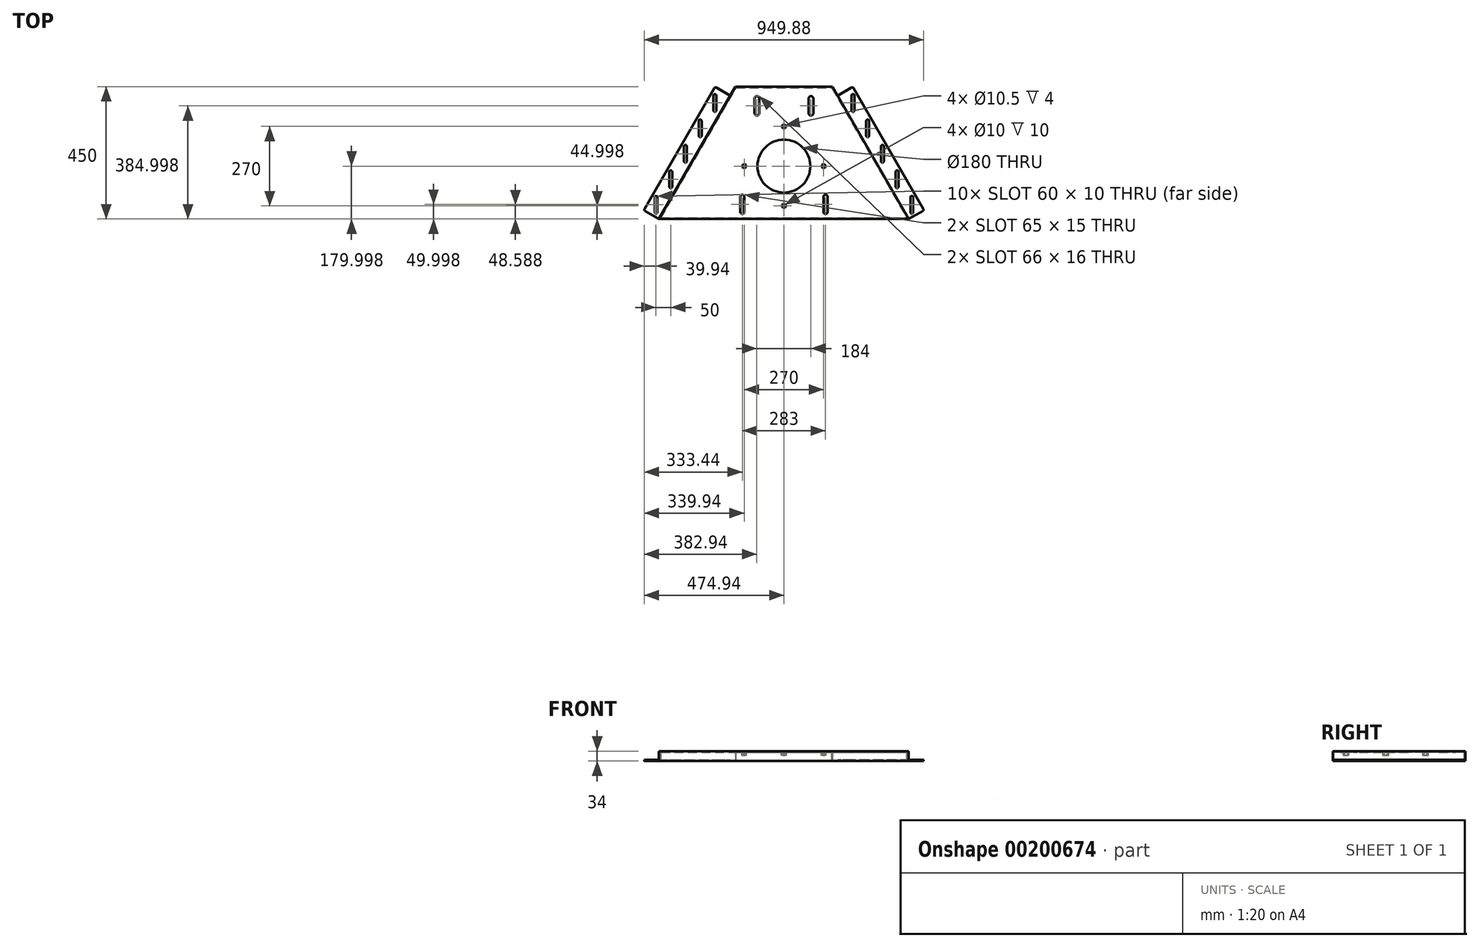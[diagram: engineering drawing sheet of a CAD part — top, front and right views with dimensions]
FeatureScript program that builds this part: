
annotation { "Feature Type Name" : "Feature", "Feature Type Description" : "" }
export const myFeature = defineFeature(function(context is Context, id is Id, definition is map)
    precondition{}
    {
        {
            var Q0;
            Q0=qCreatedBy(makeId("Top.planeOp"),FACE);
            var sketch = newSketch(context, id + "F0", { "sketchPlane" : qUnion([Q0])});
            skLineSegment(sketch, "E0.bottom", {"start": v(0, -344.4) * mm, "end": v(-424.8, -344.4) * mm});
            skLineSegment(sketch, "E0.top", {"start": v(0, 105.6) * mm, "end": v(-165, 105.6) * mm});
            skLineSegment(sketch, "E0.right", {"start": v(-424.8, -344.4) * mm, "end": v(-165, 105.6) * mm});
            skPoint(sketch, "E0.middle", {"position": v(0, 0) * mm});
            skLineSegment(sketch, "E1", {"start": v(0, 0) * mm, "end": v(0, 211.2) * mm, "construction": true});
            skLineSegment(sketch, "E2.MirrorCS", {"start": v(0, 105.6) * mm, "end": v(165, 105.6) * mm});
            skLineSegment(sketch, "E3.MirrorCS", {"start": v(424.8, -344.4) * mm, "end": v(165, 105.6) * mm});
            skLineSegment(sketch, "E4.MirrorCS", {"start": v(0, -344.4) * mm, "end": v(424.8, -344.4) * mm});
            skSolve(sketch);
        }
        {
            var Q0;
            Q0 = qSketchRegion(id + "F0", true);
            extrude(context, id + "F1", {"entities" : qUnion([Q0]), "depth" : 4 * mm});
        }
        {
            var Q0;
            Q0=makeQuery(id+"F1.opExtrude","CAP_FACE",FACE,{"disambiguationData":[OSD([sQuery(id+"F0.wireOp",EDGE,"E0.bottom"),sQuery(id+"F0.wireOp",EDGE,"E0.top"),sQuery(id+"F0.wireOp",EDGE,"E0.left"),sQuery(id+"F0.wireOp",EDGE,"E0.right")])],"isStart":false});
            var sketch = newSketch(context, id + "F2", { "sketchPlane" : qUnion([Q0])});
            skLineSegment(sketch, "E5", {"start": v(0, 105.6) * mm, "end": v(0, -344.4) * mm, "construction": true});
            skCircle(sketch, "E6", {"center": v(0, -29.4) * mm, "radius": 5.25 * mm});
            skLineSegment(sketch, "E7", {"start": v(-320.88, -164.4) * mm, "end": v(320.88, -164.4) * mm, "construction": true});
            skCircle(sketch, "E8.MirrorC", {"center": v(0, -299.4) * mm, "radius": 5.25 * mm});
            skCircle(sketch, "E9", {"center": v(-135, -164.4) * mm, "radius": 5.25 * mm});
            skCircle(sketch, "E10.MirrorC", {"center": v(135, -164.4) * mm, "radius": 5.25 * mm});
            skCircle(sketch, "E11", {"center": v(0, -164.4) * mm, "radius": 90 * mm});
            skLineSegment(sketch, "E12.bottom", {"start": v(-84, 15.6) * mm, "end": v(-100, 15.6) * mm});
            skLineSegment(sketch, "E12.top", {"start": v(-84, 65.6) * mm, "end": v(-100, 65.6) * mm});
            skLineSegment(sketch, "E12.left", {"start": v(-84, 15.6) * mm, "end": v(-84, 65.6) * mm});
            skLineSegment(sketch, "E12.right", {"start": v(-100, 15.6) * mm, "end": v(-100, 65.6) * mm});
            skPoint(sketch, "E12.middle", {"position": v(-92, 40.6) * mm});
            skLineSegment(sketch, "E13.MirrorCS", {"start": v(84, 15.6) * mm, "end": v(100, 15.6) * mm});
            skLineSegment(sketch, "E14.MirrorCS", {"start": v(84, 65.6) * mm, "end": v(100, 65.6) * mm});
            skLineSegment(sketch, "E15.MirrorCS", {"start": v(100, 15.6) * mm, "end": v(100, 65.6) * mm});
            skLineSegment(sketch, "E16.MirrorCS", {"start": v(84, 15.6) * mm, "end": v(84, 65.6) * mm});
            skPoint(sketch, "E17.MirrorP", {"position": v(92, 40.6) * mm});
            skArc(sketch, "E18", {"start": v(-84, 65.6) * mm, "mid": v(-92, 73.6) * mm, "end": v(-100, 65.6) * mm});
            skArc(sketch, "E19", {"start": v(-100, 15.6) * mm, "mid": v(-92, 7.6) * mm, "end": v(-84, 15.6) * mm});
            skArc(sketch, "E20.MirrorCS", {"start": v(84, 65.6) * mm, "mid": v(92, 73.6) * mm, "end": v(100, 65.6) * mm});
            skArc(sketch, "E21.MirrorCS", {"start": v(100, 15.6) * mm, "mid": v(92, 7.6) * mm, "end": v(84, 15.6) * mm});
            skSolve(sketch);
        }
        {
            var Q0;
            Q0 = qSketchRegion(id + "F2", true);
            extrude(context, id + "F3", {"entities" : qUnion([Q0]), "operationType" : NewBodyOperationType.REMOVE, "oppositeDirection" : true, "depth" : 25 * mm});
        }
        {
            var Q0;
            Q0=makeQuery(id+"F1.opExtrude","CAP_FACE",FACE,{"disambiguationData":[OSD([sQuery(id+"F0.wireOp",EDGE,"E0.bottom"),sQuery(id+"F0.wireOp",EDGE,"E0.top"),sQuery(id+"F0.wireOp",EDGE,"E0.left"),sQuery(id+"F0.wireOp",EDGE,"E0.right")])],"isStart":true});
            var sketch = newSketch(context, id + "F4", { "sketchPlane" : qUnion([Q0])});
            skLineSegment(sketch, "E22.bottom", {"start": v(-165, -105.6) * mm, "end": v(165, -105.6) * mm});
            skLineSegment(sketch, "E22.top", {"start": v(-165, -101.6) * mm, "end": v(165, -101.6) * mm});
            skLineSegment(sketch, "E22.left", {"start": v(-165, -105.6) * mm, "end": v(-165, -101.6) * mm});
            skLineSegment(sketch, "E22.right", {"start": v(165, -105.6) * mm, "end": v(165, -101.6) * mm});
            skLineSegment(sketch, "E23.bottom", {"start": v(-424.8, 344.4) * mm, "end": v(424.8, 344.4) * mm});
            skLineSegment(sketch, "E23.top", {"start": v(-422.5, 340.4) * mm, "end": v(422.5, 340.4) * mm});
            skLineSegment(sketch, "E23.left", {"start": v(-424.8, 344.4) * mm, "end": v(-422.5, 340.4) * mm});
            skLineSegment(sketch, "E24.bottom", {"start": v(-423.65, 342.4) * mm, "end": v(-420.19, 344.4) * mm});
            skLineSegment(sketch, "E24.top", {"start": v(-165, -105.6) * mm, "end": v(-161.54, -103.6) * mm});
            skLineSegment(sketch, "E24.left", {"start": v(-423.65, 342.4) * mm, "end": v(-165, -105.6) * mm});
            skLineSegment(sketch, "E24.right", {"start": v(-420.19, 344.4) * mm, "end": v(-161.54, -103.6) * mm});
            skLineSegment(sketch, "E25.bottom", {"start": v(161.54, -103.6) * mm, "end": v(165, -105.6) * mm});
            skLineSegment(sketch, "E25.left", {"start": v(165, -105.6) * mm, "end": v(424.8, 344.4) * mm});
            skLineSegment(sketch, "E25.right", {"start": v(161.54, -103.6) * mm, "end": v(420.19, 344.4) * mm});
            skSolve(sketch);
        }
        {
            var Q0;
            Q0 = qSketchRegion(id + "F4", true);
            extrude(context, id + "F5", {"entities" : qUnion([Q0]), "operationType" : NewBodyOperationType.ADD, "depth" : 30 * mm});
        }
        {
            var Q0;
            Q0=makeQuery(id+"F5.opExtrude","CAP_FACE",FACE,{"disambiguationData":[OSD([sQuery(id+"F4.wireOp",EDGE,"E22.bottom"),sQuery(id+"F4.wireOp",EDGE,"E22.top"),sQuery(id+"F4.wireOp",EDGE,"E23.bottom"),sQuery(id+"F4.wireOp",EDGE,"E23.top"),sQuery(id+"F4.wireOp",EDGE,"E23.left"),sQuery(id+"F4.wireOp",EDGE,"E23.right"),sQuery(id+"F4.wireOp",EDGE,"E24.bottom"),sQuery(id+"F4.wireOp",EDGE,"E24.left"),sQuery(id+"F4.wireOp",EDGE,"E24.right"),sQuery(id+"F4.wireOp",EDGE,"E25.top"),sQuery(id+"F4.wireOp",EDGE,"E25.left"),sQuery(id+"F4.wireOp",EDGE,"E25.right")])],"isStart":false});
            var sketch = newSketch(context, id + "F6", { "sketchPlane" : qUnion([Q0])});
            skLineSegment(sketch, "E26.bottom", {"start": v(-476.77, 314.4) * mm, "end": v(-424.8, 344.4) * mm});
            skLineSegment(sketch, "E26.top", {"start": v(-234.28, -105.6) * mm, "end": v(-182.32, -75.6) * mm});
            skLineSegment(sketch, "E26.left", {"start": v(-476.77, 314.4) * mm, "end": v(-234.28, -105.6) * mm});
            skLineSegment(sketch, "E26.right", {"start": v(-424.8, 344.4) * mm, "end": v(-182.32, -75.6) * mm});
            skLineSegment(sketch, "E27", {"start": v(-165, -105.6) * mm, "end": v(-269.69, -105.6) * mm, "construction": true});
            skLineSegment(sketch, "E28", {"start": v(0, 340.4) * mm, "end": v(0, 72.27) * mm, "construction": true});
            skPoint(sketch, "E28.endSnap0", {"position": v(0, -101.6) * mm});
            skLineSegment(sketch, "E29.MirrorCS", {"start": v(476.77, 314.4) * mm, "end": v(234.28, -105.6) * mm});
            skLineSegment(sketch, "E30.MirrorCS", {"start": v(424.8, 344.4) * mm, "end": v(182.32, -75.6) * mm});
            skLineSegment(sketch, "E31.MirrorCS", {"start": v(234.28, -105.6) * mm, "end": v(182.32, -75.6) * mm});
            skLineSegment(sketch, "E32.MirrorCS", {"start": v(476.77, 314.4) * mm, "end": v(424.8, 344.4) * mm});
            skSolve(sketch);
        }
        {
            var Q0;
            Q0 = qSketchRegion(id + "F6", true);
            extrude(context, id + "F7", {"entities" : qUnion([Q0]), "operationType" : NewBodyOperationType.ADD, "oppositeDirection" : true, "depth" : 4 * mm});
        }
        {
            var Q0;
            Q0=makeQuery(id+"F7.boolean.opBoolean","MERGE",FACE,{"derivedFrom":[makeQuery(id+"F5.opExtrude","CAP_FACE",FACE,{"disambiguationData":[OSD([sQuery(id+"F4.wireOp",EDGE,"E22.bottom"),sQuery(id+"F4.wireOp",EDGE,"E22.top"),sQuery(id+"F4.wireOp",EDGE,"E23.bottom"),sQuery(id+"F4.wireOp",EDGE,"E23.top"),sQuery(id+"F4.wireOp",EDGE,"E23.left"),sQuery(id+"F4.wireOp",EDGE,"E23.right"),sQuery(id+"F4.wireOp",EDGE,"E24.bottom"),sQuery(id+"F4.wireOp",EDGE,"E24.left"),sQuery(id+"F4.wireOp",EDGE,"E24.right"),sQuery(id+"F4.wireOp",EDGE,"E25.top"),sQuery(id+"F4.wireOp",EDGE,"E25.left"),sQuery(id+"F4.wireOp",EDGE,"E25.right")])],"isStart":false}),makeQuery(id+"F7.opExtrude","CAP_FACE",FACE,{"disambiguationData":[OSD([sQuery(id+"F6.wireOp",EDGE,"E26.bottom"),sQuery(id+"F6.wireOp",EDGE,"E26.top"),sQuery(id+"F6.wireOp",EDGE,"E26.left"),sQuery(id+"F6.wireOp",EDGE,"E26.right")])],"isStart":true}),makeQuery(id+"F7.opExtrude","CAP_FACE",FACE,{"disambiguationData":[OSD([sQuery(id+"F6.wireOp",EDGE,"E29.MirrorCS"),sQuery(id+"F6.wireOp",EDGE,"E30.MirrorCS"),sQuery(id+"F6.wireOp",EDGE,"E31.MirrorCS"),sQuery(id+"F6.wireOp",EDGE,"E32.MirrorCS")])],"isStart":true})]});
            var sketch = newSketch(context, id + "F8", { "sketchPlane" : qUnion([Q0])});
            skLineSegment(sketch, "E33", {"start": v(0, 340.4) * mm, "end": v(0, 48.41) * mm, "construction": true});
            skLineSegment(sketch, "E34.MirrorCS", {"start": v(-230, -75.6) * mm, "end": v(-240, -75.6) * mm});
            skLineSegment(sketch, "E35.MirrorCS", {"start": v(-240, -25.6) * mm, "end": v(-230, -25.6) * mm});
            skLineSegment(sketch, "E36.MirrorCS", {"start": v(-230, -75.6) * mm, "end": v(-230, -25.6) * mm});
            skLineSegment(sketch, "E37.MirrorCS", {"start": v(-240, -75.6) * mm, "end": v(-240, -25.6) * mm});
            skLineSegment(sketch, "E38", {"start": v(-165, -105.6) * mm, "end": v(-165, 11.41) * mm, "construction": true});
            skArc(sketch, "E39", {"start": v(-240, -75.6) * mm, "mid": v(-235, -80.6) * mm, "end": v(-230, -75.6) * mm});
            skArc(sketch, "E40", {"start": v(-230, -25.6) * mm, "mid": v(-235, -20.6) * mm, "end": v(-240, -25.6) * mm});
            skCircle(sketch, "E41.0", {"center": v(0, 29.4) * mm, "radius": 5.25 * mm});
            skLineSegment(sketch, "E42", {"start": v(-355.53, 104.4) * mm, "end": v(-259.8, 159.67) * mm, "construction": true});
            skLineSegment(sketch, "E43", {"start": v(-235, -75.6) * mm, "end": v(-235, -25.6) * mm, "construction": true});
            skPoint(sketch, "E44", {"position": v(-235, -50.6) * mm});
            skLineSegment(sketch, "E45.1.0.0", {"start": v(-280, 11) * mm, "end": v(-280, 61) * mm});
            skLineSegment(sketch, "E45.1.0.1", {"start": v(-290, 11) * mm, "end": v(-290, 61) * mm});
            skArc(sketch, "E45.1.0.2", {"start": v(-280, 61) * mm, "mid": v(-285, 66) * mm, "end": v(-290, 61) * mm});
            skArc(sketch, "E45.1.0.3", {"start": v(-290, 11) * mm, "mid": v(-285, 6) * mm, "end": v(-280, 11) * mm});
            skPoint(sketch, "E45.1.0.4", {"position": v(-285, 36) * mm});
            skLineSegment(sketch, "E45.2.0.0", {"start": v(-330, 97.6) * mm, "end": v(-330, 147.6) * mm});
            skLineSegment(sketch, "E45.2.0.1", {"start": v(-340, 97.6) * mm, "end": v(-340, 147.6) * mm});
            skArc(sketch, "E45.2.0.2", {"start": v(-330, 147.6) * mm, "mid": v(-335, 152.6) * mm, "end": v(-340, 147.6) * mm});
            skArc(sketch, "E45.2.0.3", {"start": v(-340, 97.6) * mm, "mid": v(-335, 92.6) * mm, "end": v(-330, 97.6) * mm});
            skPoint(sketch, "E45.2.0.4", {"position": v(-335, 122.6) * mm});
            skLineSegment(sketch, "E45.3.0.0", {"start": v(-380, 184.2) * mm, "end": v(-380, 234.2) * mm});
            skLineSegment(sketch, "E45.3.0.1", {"start": v(-390, 184.2) * mm, "end": v(-390, 234.2) * mm});
            skArc(sketch, "E45.3.0.2", {"start": v(-380, 234.2) * mm, "mid": v(-385, 239.2) * mm, "end": v(-390, 234.2) * mm});
            skArc(sketch, "E45.3.0.3", {"start": v(-390, 184.2) * mm, "mid": v(-385, 179.2) * mm, "end": v(-380, 184.2) * mm});
            skPoint(sketch, "E45.3.0.4", {"position": v(-385, 209.2) * mm});
            skLineSegment(sketch, "E45.direction1", {"start": v(-240, -75.6) * mm, "end": v(-290, 11) * mm, "construction": true});
            skLineSegment(sketch, "E46.0.4.0", {"start": v(-430, 270.81) * mm, "end": v(-430, 320.81) * mm});
            skLineSegment(sketch, "E46.3.4.0", {"start": v(-440, 270.81) * mm, "end": v(-440, 320.81) * mm});
            skArc(sketch, "E46.6.4.0", {"start": v(-430, 320.81) * mm, "mid": v(-435, 325.81) * mm, "end": v(-440, 320.81) * mm});
            skArc(sketch, "E46.10.4.0", {"start": v(-440, 270.81) * mm, "mid": v(-435, 265.81) * mm, "end": v(-430, 270.81) * mm});
            skPoint(sketch, "E46.14.4.0", {"position": v(-435, 295.81) * mm});
            skArc(sketch, "E47.MirrorCS", {"start": v(390, 184.2) * mm, "mid": v(385, 179.2) * mm, "end": v(380, 184.2) * mm});
            skArc(sketch, "E48.MirrorCS", {"start": v(380, 234.2) * mm, "mid": v(385, 239.2) * mm, "end": v(390, 234.2) * mm});
            skArc(sketch, "E49.MirrorCS", {"start": v(440, 270.81) * mm, "mid": v(435, 265.81) * mm, "end": v(430, 270.81) * mm});
            skArc(sketch, "E50.MirrorCS", {"start": v(430, 320.81) * mm, "mid": v(435, 325.81) * mm, "end": v(440, 320.81) * mm});
            skLineSegment(sketch, "E51.MirrorCS", {"start": v(430, 270.81) * mm, "end": v(430, 320.81) * mm});
            skLineSegment(sketch, "E52.MirrorCS", {"start": v(390, 184.2) * mm, "end": v(390, 234.2) * mm});
            skLineSegment(sketch, "E53.MirrorCS", {"start": v(440, 270.81) * mm, "end": v(440, 320.81) * mm});
            skPoint(sketch, "E54.MirrorP", {"position": v(435, 295.81) * mm});
            skPoint(sketch, "E55.MirrorP", {"position": v(385, 209.2) * mm});
            skArc(sketch, "E56.MirrorCS", {"start": v(330, 147.6) * mm, "mid": v(335, 152.6) * mm, "end": v(340, 147.6) * mm});
            skArc(sketch, "E57.MirrorCS", {"start": v(340, 97.6) * mm, "mid": v(335, 92.6) * mm, "end": v(330, 97.6) * mm});
            skLineSegment(sketch, "E58.MirrorCS", {"start": v(380, 184.2) * mm, "end": v(380, 234.2) * mm});
            skLineSegment(sketch, "E59.MirrorCS", {"start": v(340, 97.6) * mm, "end": v(340, 147.6) * mm});
            skLineSegment(sketch, "E60.MirrorCS", {"start": v(330, 97.6) * mm, "end": v(330, 147.6) * mm});
            skPoint(sketch, "E61.MirrorP", {"position": v(335, 122.6) * mm});
            skLineSegment(sketch, "E62.MirrorCS", {"start": v(230, -75.6) * mm, "end": v(240, -75.6) * mm});
            skArc(sketch, "E63.MirrorCS", {"start": v(240, -75.6) * mm, "mid": v(235, -80.6) * mm, "end": v(230, -75.6) * mm});
            skLineSegment(sketch, "E64.MirrorCS", {"start": v(240, -25.6) * mm, "end": v(230, -25.6) * mm});
            skArc(sketch, "E65.MirrorCS", {"start": v(290, 11) * mm, "mid": v(285, 6) * mm, "end": v(280, 11) * mm});
            skArc(sketch, "E66.MirrorCS", {"start": v(230, -25.6) * mm, "mid": v(235, -20.6) * mm, "end": v(240, -25.6) * mm});
            skArc(sketch, "E67.MirrorCS", {"start": v(280, 61) * mm, "mid": v(285, 66) * mm, "end": v(290, 61) * mm});
            skLineSegment(sketch, "E68.MirrorCS", {"start": v(240, -75.6) * mm, "end": v(240, -25.6) * mm});
            skLineSegment(sketch, "E69.MirrorCS", {"start": v(230, -75.6) * mm, "end": v(230, -25.6) * mm});
            skLineSegment(sketch, "E70.MirrorCS", {"start": v(280, 11) * mm, "end": v(280, 61) * mm});
            skLineSegment(sketch, "E71.MirrorCS", {"start": v(235, -75.6) * mm, "end": v(235, -25.6) * mm, "construction": true});
            skLineSegment(sketch, "E72.MirrorCS", {"start": v(290, 11) * mm, "end": v(290, 61) * mm});
            skPoint(sketch, "E73.MirrorP", {"position": v(285, 36) * mm});
            skPoint(sketch, "E74.MirrorP", {"position": v(235, -50.6) * mm});
            skSolve(sketch);
        }
        {
            var Q0;
            Q0 = qSketchRegion(id + "F8", true);
            extrude(context, id + "F9", {"entities" : qUnion([Q0]), "operationType" : NewBodyOperationType.REMOVE, "endBound" : BoundingType.THROUGH_ALL, "oppositeDirection" : true, "depth" : 25 * mm});
        }
        {
            var Q0;
            Q0=makeQuery(id+"F7.opExtrude","SWEPT_EDGE",EDGE,{"disambiguationData":[OSD([sQuery(id+"F6.wireOp",EDGE,"E26.bottom"),sQuery(id+"F6.wireOp",EDGE,"E26.left")])]});
            var Q1;
            Q1=makeQuery(id+"F7.opExtrude","SWEPT_EDGE",EDGE,{"disambiguationData":[OSD([sQuery(id+"F6.wireOp",EDGE,"E26.top"),sQuery(id+"F6.wireOp",EDGE,"E26.left")])]});
            var Q2;
            Q2=makeQuery(id+"F7.opExtrude","SWEPT_EDGE",EDGE,{"disambiguationData":[OSD([sQuery(id+"F6.wireOp",EDGE,"E29.MirrorCS"),sQuery(id+"F6.wireOp",EDGE,"E31.MirrorCS")])]});
            var Q3;
            Q3=makeQuery(id+"F7.opExtrude","SWEPT_EDGE",EDGE,{"disambiguationData":[OSD([sQuery(id+"F6.wireOp",EDGE,"E29.MirrorCS"),sQuery(id+"F6.wireOp",EDGE,"E32.MirrorCS")])]});
            fillet(context, id + "F10", {"entities" : qUnion([Q0, Q1, Q2, Q3]), "radius" : 5 * mm, "tangentPropagation" : true, "allowEdgeOverflow" : false});
        }
        {
            var Q0;
            Q0=makeQuery(id+"F1.opExtrude","CAP_FACE",FACE,{"disambiguationData":[OSD([sQuery(id+"F0.wireOp",EDGE,"E0.bottom"),sQuery(id+"F0.wireOp",EDGE,"E0.top"),sQuery(id+"F0.wireOp",EDGE,"E0.right"),sQuery(id+"F0.wireOp",EDGE,"E2.MirrorCS"),sQuery(id+"F0.wireOp",EDGE,"E3.MirrorCS"),sQuery(id+"F0.wireOp",EDGE,"E4.MirrorCS")])],"isStart":true});
            var sketch = newSketch(context, id + "F11", { "sketchPlane" : qUnion([Q0])});
            skCircle(sketch, "E75.cCircle", {"center": v(-135, 164.4) * mm, "radius": 9.81 * mm, "construction": true});
            skLineSegment(sketch, "E75.0", {"start": v(-126.5, 159.5) * mm, "end": v(-135, 154.59) * mm});
            skLineSegment(sketch, "E75.1", {"start": v(-135, 154.59) * mm, "end": v(-143.5, 159.5) * mm});
            skLineSegment(sketch, "E75.2", {"start": v(-143.5, 159.5) * mm, "end": v(-143.5, 169.3) * mm});
            skLineSegment(sketch, "E75.3", {"start": v(-143.5, 169.3) * mm, "end": v(-135, 174.22) * mm});
            skLineSegment(sketch, "E75.4", {"start": v(-135, 174.22) * mm, "end": v(-126.5, 169.3) * mm});
            skLineSegment(sketch, "E75.5", {"start": v(-126.5, 169.3) * mm, "end": v(-126.5, 159.5) * mm});
            skCircle(sketch, "E76.cCircle", {"center": v(135, 164.4) * mm, "radius": 9.81 * mm, "construction": true});
            skLineSegment(sketch, "E76.0", {"start": v(135, 154.59) * mm, "end": v(126.5, 159.5) * mm});
            skLineSegment(sketch, "E76.1", {"start": v(126.5, 159.5) * mm, "end": v(126.5, 169.3) * mm});
            skLineSegment(sketch, "E76.2", {"start": v(126.5, 169.3) * mm, "end": v(135, 174.22) * mm});
            skLineSegment(sketch, "E76.3", {"start": v(135, 174.22) * mm, "end": v(143.5, 169.3) * mm});
            skLineSegment(sketch, "E76.4", {"start": v(143.5, 169.3) * mm, "end": v(143.5, 159.5) * mm});
            skLineSegment(sketch, "E76.5", {"start": v(143.5, 159.5) * mm, "end": v(135, 154.59) * mm});
            skCircle(sketch, "E77.cCircle", {"center": v(0, 299.4) * mm, "radius": 9.81 * mm, "construction": true});
            skLineSegment(sketch, "E77.0", {"start": v(0, 289.59) * mm, "end": v(-8.5, 294.5) * mm});
            skLineSegment(sketch, "E77.1", {"start": v(-8.5, 294.5) * mm, "end": v(-8.5, 304.3) * mm});
            skLineSegment(sketch, "E77.2", {"start": v(-8.5, 304.3) * mm, "end": v(0, 309.22) * mm});
            skLineSegment(sketch, "E77.3", {"start": v(0, 309.22) * mm, "end": v(8.5, 304.3) * mm});
            skLineSegment(sketch, "E77.4", {"start": v(8.5, 304.3) * mm, "end": v(8.5, 294.5) * mm});
            skLineSegment(sketch, "E77.5", {"start": v(8.5, 294.5) * mm, "end": v(0, 289.59) * mm});
            skCircle(sketch, "E78.cCircle", {"center": v(0, 29.4) * mm, "radius": 9.81 * mm, "construction": true});
            skLineSegment(sketch, "E78.0", {"start": v(8.5, 24.5) * mm, "end": v(0, 19.59) * mm});
            skLineSegment(sketch, "E78.1", {"start": v(0, 19.59) * mm, "end": v(-8.5, 24.5) * mm});
            skLineSegment(sketch, "E78.2", {"start": v(-8.5, 24.5) * mm, "end": v(-8.5, 34.3) * mm});
            skLineSegment(sketch, "E78.3", {"start": v(-8.5, 34.3) * mm, "end": v(0, 39.22) * mm});
            skLineSegment(sketch, "E78.4", {"start": v(0, 39.22) * mm, "end": v(8.5, 34.3) * mm});
            skLineSegment(sketch, "E78.5", {"start": v(8.5, 34.3) * mm, "end": v(8.5, 24.5) * mm});
            skCircle(sketch, "E79", {"center": v(-135, 164.4) * mm, "radius": 5 * mm});
            skCircle(sketch, "E80", {"center": v(0, 29.4) * mm, "radius": 5 * mm});
            skCircle(sketch, "E81", {"center": v(135, 164.4) * mm, "radius": 5 * mm});
            skCircle(sketch, "E82", {"center": v(0, 299.4) * mm, "radius": 5 * mm});
            skSolve(sketch);
        }
        {
            var Q0;
            Q0 = qSketchRegion(id + "F11", true);
            extrude(context, id + "F12", {"entities" : qUnion([Q0]), "operationType" : NewBodyOperationType.ADD, "depth" : 10 * mm});
        }
        {
            var Q0;
            Q0=makeQuery(id+"F1.opExtrude","CAP_FACE",FACE,{"disambiguationData":[OSD([sQuery(id+"F0.wireOp",EDGE,"E0.bottom"),sQuery(id+"F0.wireOp",EDGE,"E0.top"),sQuery(id+"F0.wireOp",EDGE,"E0.left"),sQuery(id+"F0.wireOp",EDGE,"E0.right")])],"isStart":false});
            var sketch = newSketch(context, id + "F13", { "sketchPlane" : qUnion([Q0])});
            skLineSegment(sketch, "E83", {"start": v(0, -344.4) * mm, "end": v(0, 79.38) * mm, "construction": true});
            skLineSegment(sketch, "E84.bottom", {"start": v(-134, -319.4) * mm, "end": v(-149, -319.4) * mm});
            skLineSegment(sketch, "E84.top", {"start": v(-134, -269.4) * mm, "end": v(-149, -269.4) * mm});
            skLineSegment(sketch, "E84.left", {"start": v(-134, -319.4) * mm, "end": v(-134, -269.4) * mm});
            skLineSegment(sketch, "E84.right", {"start": v(-149, -319.4) * mm, "end": v(-149, -269.4) * mm});
            skPoint(sketch, "E84.middle", {"position": v(-141.5, -294.4) * mm});
            skArc(sketch, "E85", {"start": v(-134, -269.4) * mm, "mid": v(-141.5, -261.9) * mm, "end": v(-149, -269.4) * mm});
            skArc(sketch, "E86", {"start": v(-149, -319.4) * mm, "mid": v(-141.5, -326.9) * mm, "end": v(-134, -319.4) * mm});
            skArc(sketch, "E87.MirrorCS", {"start": v(134, -269.4) * mm, "mid": v(141.5, -261.9) * mm, "end": v(149, -269.4) * mm});
            skArc(sketch, "E88.MirrorCS", {"start": v(149, -319.4) * mm, "mid": v(141.5, -326.9) * mm, "end": v(134, -319.4) * mm});
            skLineSegment(sketch, "E89.MirrorCS", {"start": v(134, -319.4) * mm, "end": v(134, -269.4) * mm});
            skLineSegment(sketch, "E90.MirrorCS", {"start": v(149, -319.4) * mm, "end": v(149, -269.4) * mm});
            skPoint(sketch, "E91", {"position": v(-135, -164.4) * mm});
            skSolve(sketch);
        }
        {
            var Q0;
            Q0 = qSketchRegion(id + "F13", true);
            extrude(context, id + "F14", {"entities" : qUnion([Q0]), "operationType" : NewBodyOperationType.REMOVE, "endBound" : BoundingType.THROUGH_ALL, "oppositeDirection" : true, "depth" : 25 * mm});
        }
    });
